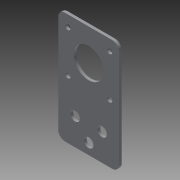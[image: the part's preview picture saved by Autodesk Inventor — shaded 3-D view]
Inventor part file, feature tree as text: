
AUTODESK INVENTOR PART (.ipt)
format: ipt  version: 2015 SP1 (Build 190203100, 203)  size: 115,712 bytes
history: native  units: in
note: dims shown in document units (in); Inventor stores cm internally (conversion verified against a paired STEP export)
features: extrude x1
ambient origin geometry x8: Origin, YZ Plane, XZ Plane, XY Plane, X Axis, Y Axis, Z Axis, Center Point
bodies: Body1 (feature_tree)
feature tree (1):
  extrude  "Extrusion4"  Depth=0.8661in
